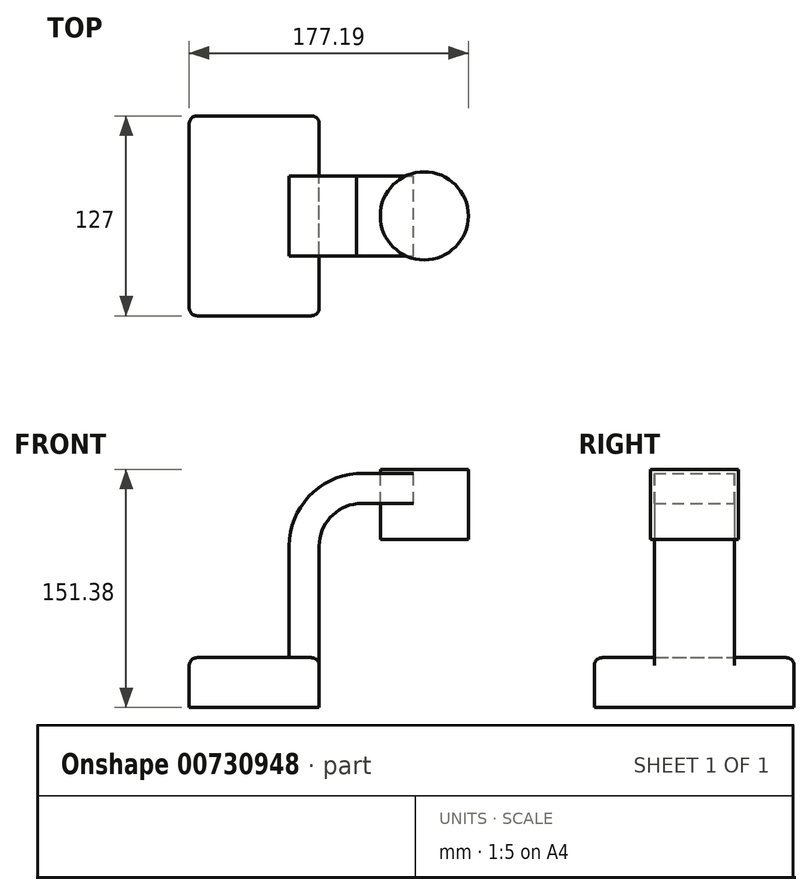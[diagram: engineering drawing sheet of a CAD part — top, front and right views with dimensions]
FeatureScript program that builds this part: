
annotation { "Feature Type Name" : "Feature", "Feature Type Description" : "" }
export const myFeature = defineFeature(function(context is Context, id is Id, definition is map)
    precondition{}
    {
        {
            var Q0;
            Q0=qCreatedBy(makeId("Front.planeOp"),FACE);
            var sketch = newSketch(context, id + "F0", { "sketchPlane" : qUnion([Q0])});
            skLineSegment(sketch, "E0.bottom", {"start": v(-41.27, -15.88) * mm, "end": v(41.28, -15.88) * mm});
            skLineSegment(sketch, "E0.top", {"start": v(-41.28, 15.88) * mm, "end": v(41.27, 15.88) * mm});
            skLineSegment(sketch, "E0.left", {"start": v(-41.27, -15.88) * mm, "end": v(-41.28, 15.88) * mm});
            skLineSegment(sketch, "E0.right", {"start": v(41.28, -15.88) * mm, "end": v(41.27, 15.88) * mm});
            skPoint(sketch, "E0.middle", {"position": v(0, 0) * mm});
            skLineSegment(sketch, "E1.bottom", {"start": v(80.04, 90.8) * mm, "end": v(135.92, 90.8) * mm});
            skLineSegment(sketch, "E1.top", {"start": v(80.04, 135.5) * mm, "end": v(135.92, 135.5) * mm});
            skLineSegment(sketch, "E1.left", {"start": v(80.04, 90.8) * mm, "end": v(80.04, 135.5) * mm});
            skLineSegment(sketch, "E1.right", {"start": v(135.92, 90.8) * mm, "end": v(135.92, 135.5) * mm});
            skPoint(sketch, "E1.middle", {"position": v(107.98, 113.15) * mm});
            skLineSegment(sketch, "E2", {"start": v(41.27, 15.88) * mm, "end": v(41.27, 86.74) * mm});
            skArc(sketch, "E3", {"start": v(41.27, 86.74) * mm, "mid": v(48.28, 104.9) * mm, "end": v(65.67, 113.67) * mm});
            skLineSegment(sketch, "E4", {"start": v(65.67, 113.67) * mm, "end": v(101.16, 113.67) * mm});
            skLineSegment(sketch, "E5.0", {"start": v(64.85, 132.72) * mm, "end": v(101.16, 132.72) * mm});
            skArc(sketch, "E5.1", {"start": v(22.22, 86.74) * mm, "mid": v(34.52, 118.1) * mm, "end": v(64.85, 132.72) * mm});
            skLineSegment(sketch, "E5.2", {"start": v(22.22, 15.88) * mm, "end": v(22.22, 86.74) * mm});
            skLineSegment(sketch, "E6", {"start": v(101.16, 113.67) * mm, "end": v(101.16, 132.72) * mm});
            skFitSpline(sketch, "E7", {"points": [v(-41.28, 15.88) * mm, v(80.04, 135.5) * mm], "startDerivative": vector(12.76, 227.59) * mm, "endDerivative": vector(186.01, -1.26) * mm});
            skLineSegment(sketch, "E8", {"start": v(107.98, 113.15) * mm, "end": v(107.98, 135.5) * mm});
            skLineSegment(sketch, "E9", {"start": v(107.98, 135.5) * mm, "end": v(107.98, 90.8) * mm});
            skSolve(sketch);
        }
        {
            var Q0;
            Q0=makeQuery(id+"F0.imprint","IMPRINT",FACE,{"disambiguationData":[TD([[makeQuery(id+"F0.imprint","IMPRINT",EDGE,{"derivedFrom":sQuery(id+"F0.wireOp",EDGE,"E0.bottom")}),1.0]])]});
            extrude(context, id + "F1", {"entities" : qUnion([Q0]), "endBound" : BoundingType.SYMMETRIC, "depth" : 127 * mm, "offsetDistance" : 25.4 * mm});
        }
        {
            var Q0;
            {var subQ0=sQuery(id+"F0.wireOp",EDGE,"E2");Q0=makeQuery(id+"F0.imprint","IMPRINT",FACE,{"disambiguationData":[TD([[makeQuery(id+"F0.imprint","IMPRINT",EDGE,{"derivedFrom":subQ0}),1.0]])]});}
            var Q1;
            {var subQ5=sQuery(id+"F0.wireOp",EDGE,"E6");Q1=makeQuery(id+"F0.imprint","IMPRINT",FACE,{"disambiguationData":[TD([[makeQuery(id+"F0.imprint","IMPRINT",EDGE,{"derivedFrom":subQ5}),1.0]])]});}
            extrude(context, id + "F2", {"entities" : qUnion([Q0, Q1]), "operationType" : NewBodyOperationType.ADD, "endBound" : BoundingType.SYMMETRIC, "depth" : 50.8 * mm, "offsetDistance" : 25.4 * mm});
        }
        {
            var Q0;
            {var subQ0=sQuery(id+"F0.wireOp",EDGE,"E5.1");Q0=makeQuery(id+"F0.imprint","IMPRINT",FACE,{"disambiguationData":[TD([[makeQuery(id+"F0.imprint","IMPRINT",EDGE,{"derivedFrom":subQ0}),1.0]])]});}
            extrude(context, id + "F3", {"entities" : qUnion([Q0]), "operationType" : NewBodyOperationType.ADD, "endBound" : BoundingType.SYMMETRIC, "depth" : 15.88 * mm, "offsetDistance" : 25.4 * mm});
        }
        {
            var Q0;
            Q0=makeQuery(id+"F1.opExtrude","CAP_EDGE",EDGE,{"disambiguationData":[OSD([sQuery(id+"F0.wireOp",EDGE,"E0.top")])],"isStart":false});
            var Q1;
            Q1=makeQuery(id+"F1.opExtrude","CAP_EDGE",EDGE,{"disambiguationData":[OSD([sQuery(id+"F0.wireOp",EDGE,"E0.right")])],"isStart":false});
            var Q2;
            {var subQ0=sQuery(id+"F0.wireOp",EDGE,"E0.right");var subQ1=sQuery(id+"F0.wireOp",EDGE,"E2");var subQ2=sQuery(id+"F0.wireOp",EDGE,"E0.top");Q2=makeQuery(id+"F2.boolean.opBoolean","SPLIT",EDGE,{"disambiguationData":[TD([makeQuery(id+"F1.opExtrude","CAP_FACE",FACE,{"disambiguationData":[OSD([sQuery(id+"F0.wireOp",EDGE,"E0.bottom"),subQ2,sQuery(id+"F0.wireOp",EDGE,"E0.left"),subQ0])],"isStart":false})])],"derivedFrom":makeQuery(id+"F1.opExtrude","SWEPT_EDGE",EDGE,{"disambiguationData":[OSD([subQ2,subQ0,subQ1])]})});}
            var Q3;
            {var subQ0=sQuery(id+"F0.wireOp",EDGE,"E7");var subQ1=sQuery(id+"F0.wireOp",EDGE,"E0.top");var subQ2=sQuery(id+"F0.wireOp",EDGE,"E0.left");Q3=makeQuery(id+"F3.boolean.opBoolean","SPLIT",EDGE,{"disambiguationData":[TD([makeQuery(id+"F1.opExtrude","CAP_FACE",FACE,{"disambiguationData":[OSD([sQuery(id+"F0.wireOp",EDGE,"E0.bottom"),subQ1,subQ2,sQuery(id+"F0.wireOp",EDGE,"E0.right")])],"isStart":false})])],"derivedFrom":makeQuery(id+"F1.opExtrude","SWEPT_EDGE",EDGE,{"disambiguationData":[OSD([subQ1,subQ2,subQ0])]})});}
            var Q4;
            Q4=makeQuery(id+"F1.opExtrude","CAP_EDGE",EDGE,{"disambiguationData":[OSD([sQuery(id+"F0.wireOp",EDGE,"E0.left")])],"isStart":false});
            var Q5;
            {var subQ0=sQuery(id+"F0.wireOp",EDGE,"E7");var subQ1=sQuery(id+"F0.wireOp",EDGE,"E0.top");var subQ2=sQuery(id+"F0.wireOp",EDGE,"E0.left");Q5=makeQuery(id+"F3.boolean.opBoolean","SPLIT",EDGE,{"disambiguationData":[TD([makeQuery(id+"F1.opExtrude","CAP_FACE",FACE,{"disambiguationData":[OSD([sQuery(id+"F0.wireOp",EDGE,"E0.bottom"),subQ1,subQ2,sQuery(id+"F0.wireOp",EDGE,"E0.right")])],"isStart":true})])],"derivedFrom":makeQuery(id+"F1.opExtrude","SWEPT_EDGE",EDGE,{"disambiguationData":[OSD([subQ1,subQ2,subQ0])]})});}
            var Q6;
            Q6=makeQuery(id+"F1.opExtrude","CAP_EDGE",EDGE,{"disambiguationData":[OSD([sQuery(id+"F0.wireOp",EDGE,"E0.left")])],"isStart":true});
            var Q7;
            Q7=makeQuery(id+"F1.opExtrude","CAP_EDGE",EDGE,{"disambiguationData":[OSD([sQuery(id+"F0.wireOp",EDGE,"E0.top")])],"isStart":true});
            var Q8;
            {var subQ0=sQuery(id+"F0.wireOp",EDGE,"E2");var subQ1=sQuery(id+"F0.wireOp",EDGE,"E0.top");var subQ2=sQuery(id+"F0.wireOp",EDGE,"E0.right");Q8=makeQuery(id+"F2.boolean.opBoolean","SPLIT",EDGE,{"disambiguationData":[TD([makeQuery(id+"F1.opExtrude","CAP_FACE",FACE,{"disambiguationData":[OSD([sQuery(id+"F0.wireOp",EDGE,"E0.bottom"),subQ1,sQuery(id+"F0.wireOp",EDGE,"E0.left"),subQ2])],"isStart":true})])],"derivedFrom":makeQuery(id+"F1.opExtrude","SWEPT_EDGE",EDGE,{"disambiguationData":[OSD([subQ1,subQ2,subQ0])]})});}
            var Q9;
            Q9=makeQuery(id+"F1.opExtrude","CAP_EDGE",EDGE,{"disambiguationData":[OSD([sQuery(id+"F0.wireOp",EDGE,"E0.right")])],"isStart":true});
            fillet(context, id + "F4", {"entities" : qUnion([Q0, Q1, Q2, Q3, Q4, Q5, Q6, Q7, Q8, Q9]), "radius" : 5.08 * mm, "tangentPropagation" : true, "allowEdgeOverflow" : false});
        }
        {
            var Q0;
            {var subQ0=sQuery(id+"F0.wireOp",EDGE,"E1.right");Q0=makeQuery(id+"F0.imprint","IMPRINT",FACE,{"disambiguationData":[TD([[makeQuery(id+"F0.imprint","IMPRINT",EDGE,{"derivedFrom":subQ0}),1.0]])]});}
            var Q1;
            Q1=sQuery(id+"F0.wireOp",EDGE,"E9");
            revolve(context, id + "F5", {"surfaceOperationType" : NewSurfaceOperationType.NEW, "entities" : qUnion([Q0]), "axis" : qUnion([Q1]), "revolveType" : RevolveType.FULL});
        }
    });
